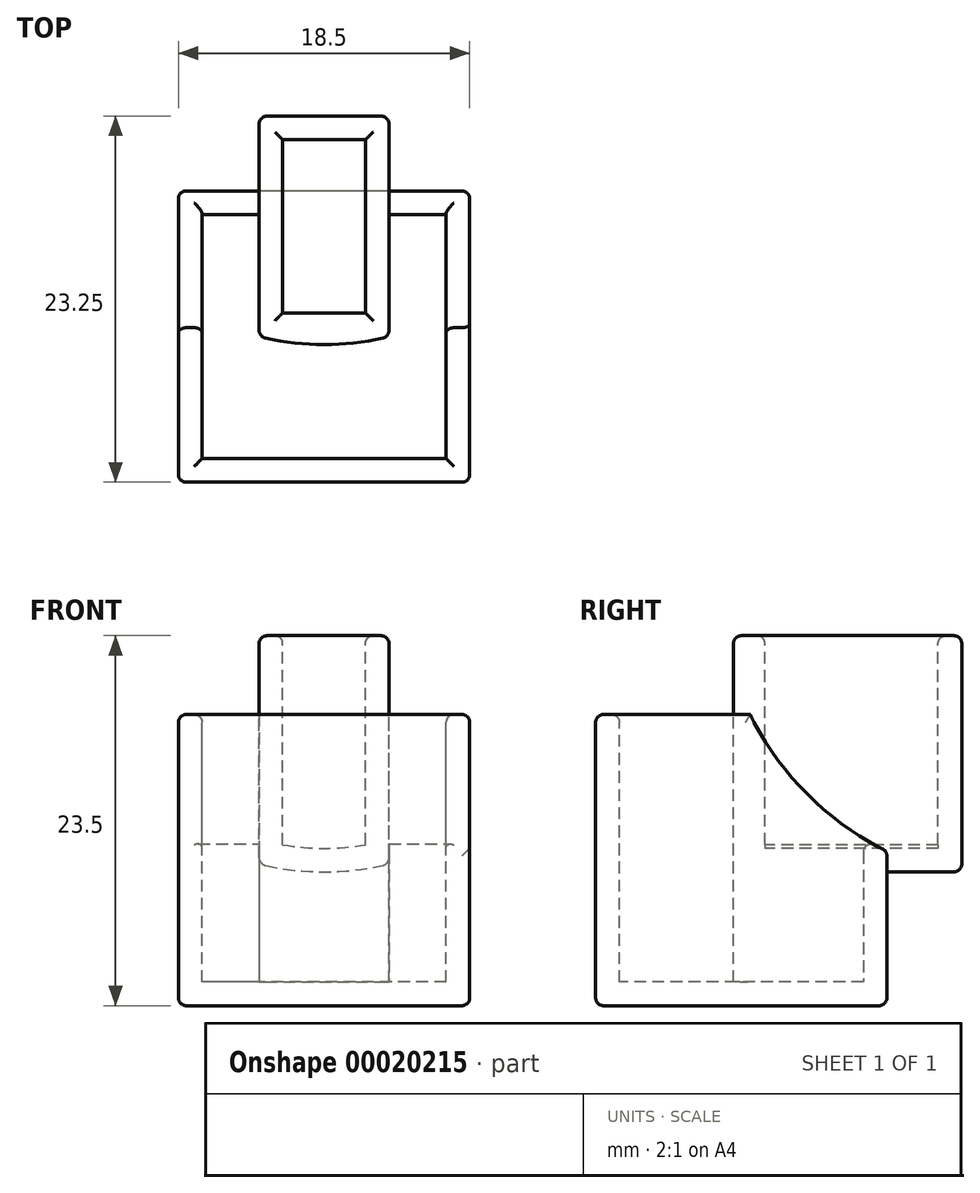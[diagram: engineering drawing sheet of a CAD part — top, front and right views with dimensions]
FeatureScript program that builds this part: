
annotation { "Feature Type Name" : "Feature", "Feature Type Description" : "" }
export const myFeature = defineFeature(function(context is Context, id is Id, definition is map)
    precondition{}
    {
        {
            var Q0;
            Q0=qCreatedBy(makeId("Top.planeOp"),FACE);
            var sketch = newSketch(context, id + "F0", { "sketchPlane" : qUnion([Q0])});
            skLineSegment(sketch, "E0.rect.bottom", {"start": v(9.25, 9.25) * mm, "end": v(-9.25, 9.25) * mm});
            skLineSegment(sketch, "E0.rect.top", {"start": v(9.25, -9.25) * mm, "end": v(-9.25, -9.25) * mm});
            skLineSegment(sketch, "E0.rect.left", {"start": v(9.25, 9.25) * mm, "end": v(9.25, -9.25) * mm});
            skLineSegment(sketch, "E0.rect.right", {"start": v(-9.25, 9.25) * mm, "end": v(-9.25, -9.25) * mm});
            skPoint(sketch, "E0.rect.middle", {"position": v(0, 0) * mm});
            skSolve(sketch);
        }
        {
            var Q0;
            Q0=makeQuery(id+"F0.imprint","IMPRINT",FACE,{"disambiguationData":[TD([[makeQuery(id+"F0.imprint","IMPRINT",EDGE,{"derivedFrom":sQuery(id+"F0.wireOp",EDGE,"E0.rect.bottom")}),1.0]])]});
            extrude(context, id + "F1", {"entities" : qUnion([Q0]), "oppositeDirection" : true, "depth" : 18.5 * mm});
        }
        {
            var Q0;
            Q0=makeQuery(id+"F1.opExtrude","SWEPT_FACE",FACE,{"disambiguationData":[OSD([sQuery(id+"F0.wireOp",EDGE,"E0.rect.left")])]});
            var sketch = newSketch(context, id + "F2", { "sketchPlane" : qUnion([Q0])});
            skPoint(sketch, "E1", {"position": v(2, 0) * mm});
            skPoint(sketch, "E2", {"position": v(-9.25, -18.5) * mm});
            skPoint(sketch, "E3", {"position": v(4.19, -5.06) * mm});
            skCircle(sketch, "E4", {"center": v(17.62, 8.37) * mm, "radius": 19 * mm});
            skSolve(sketch);
        }
        {
            var Q0;
            Q0=qSketchRegion(id+"F2",true);
            extrude(context, id + "F3", {"entities" : qUnion([Q0]), "operationType" : NewBodyOperationType.REMOVE, "oppositeDirection" : true, "depth" : 25.4 * mm});
        }
        {
            var Q0;
            Q0=makeQuery(id+"F1.opExtrude","CAP_FACE",FACE,{"disambiguationData":[OSD([sQuery(id+"F0.wireOp",EDGE,"E0.rect.bottom"),sQuery(id+"F0.wireOp",EDGE,"E0.rect.top"),sQuery(id+"F0.wireOp",EDGE,"E0.rect.left"),sQuery(id+"F0.wireOp",EDGE,"E0.rect.right")])],"isStart":true});
            var Q1;
            Q1=makeQuery(id+"F3.boolean.opBoolean","COPY",FACE,{"derivedFrom":makeQuery(id+"F3.opExtrude","SWEPT_FACE",FACE,{"disambiguationData":[OSD([sQuery(id+"F2.wireOp",EDGE,"E4")])]})});
            shell(context, id + "F4", {"entities" : qUnion([Q0, Q1]), "thickness" : 1.5 * mm});
        }
        {
            var Q0;
            Q0=qCreatedBy(makeId("Front.planeOp"),FACE);
            var sketch = newSketch(context, id + "F5", { "sketchPlane" : qUnion([Q0])});
            skPoint(sketch, "E5", {"position": v(0, 5) * mm});
            skLineSegment(sketch, "E6", {"start": v(0, 5) * mm, "end": v(0, -9.5) * mm});
            skLineSegment(sketch, "E7.top", {"start": v(4.12, 5) * mm, "end": v(-4.12, 5) * mm});
            skLineSegment(sketch, "E7.left", {"start": v(4.12, -9.5) * mm, "end": v(4.12, 5) * mm});
            skLineSegment(sketch, "E7.right", {"start": v(-4.12, -9.5) * mm, "end": v(-4.12, 5) * mm});
            skPoint(sketch, "E8", {"position": v(0, -10) * mm});
            skArc(sketch, "E9", {"start": v(-4.12, -9.5) * mm, "mid": v(0, -10) * mm, "end": v(4.13, -9.5) * mm});
            skSolve(sketch);
        }
        {
            var Q0;
            Q0=qSketchRegion(id+"F5",true);
            extrude(context, id + "F6", {"entities" : qUnion([Q0]), "operationType" : NewBodyOperationType.ADD, "oppositeDirection" : true, "depth" : 14 * mm});
        }
        {
            var Q0;
            Q0=makeQuery(id+"F6.opExtrude","SWEPT_FACE",FACE,{"disambiguationData":[OSD([sQuery(id+"F5.wireOp",EDGE,"E7.top")])]});
            shell(context, id + "F7", {"entities" : qUnion([Q0]), "thickness" : 1.5 * mm});
        }
        {
            var Q0;
            Q0=makeQuery(id+"F6.opExtrude","SWEPT_FACE",FACE,{"disambiguationData":[OSD([sQuery(id+"F5.wireOp",EDGE,"E7.top")])]});
            var sketch = newSketch(context, id + "F8", { "sketchPlane" : qUnion([Q0])});
            skArc(sketch, "E10", {"start": v(-4.13, 0) * mm, "mid": v(0, -0.5) * mm, "end": v(4.12, 0) * mm});
            skLineSegment(sketch, "E11", {"start": v(-4.13, 0) * mm, "end": v(4.12, 0) * mm});
            skSolve(sketch);
        }
        {
            var Q0;
            Q0=makeQuery(id+"F8.imprint","IMPRINT",FACE,{"disambiguationData":[TD([[makeQuery(id+"F8.imprint","IMPRINT",EDGE,{"derivedFrom":sQuery(id+"F8.wireOp",EDGE,"E10")}),1.0]])]});
            extrude(context, id + "F9", {"entities" : qUnion([Q0]), "operationType" : NewBodyOperationType.ADD, "oppositeDirection" : true, "depth" : 23.32 * mm});
        }
        {
            var Q0;
            Q0=makeQuery(id+"F9.opExtrude","SWEPT_FACE",FACE,{"disambiguationData":[OSD([sQuery(id+"F8.wireOp",EDGE,"E11")])]});
            extrude(context, id + "F10", {"entities" : qUnion([Q0]), "operationType" : NewBodyOperationType.ADD, "depth" : 8.55 * mm});
        }
        {
            var Q0;
            Q0=makeQuery(id+"F3.boolean.opBoolean","INTERSECT",EDGE,{"derivedFrom":[makeQuery(id+"F1.opExtrude","SWEPT_FACE",FACE,{"disambiguationData":[OSD([sQuery(id+"F0.wireOp",EDGE,"E0.rect.right")])]}),makeQuery(id+"F3.opExtrude","SWEPT_FACE",FACE,{"disambiguationData":[OSD([sQuery(id+"F2.wireOp",EDGE,"E4")])]})]});
            var Q1;
            Q1=makeQuery(id+"F1.opExtrude","CAP_EDGE",EDGE,{"disambiguationData":[OSD([sQuery(id+"F0.wireOp",EDGE,"E0.rect.right")])],"isStart":true});
            var Q2;
            Q2=makeQuery(id+"F1.opExtrude","SWEPT_EDGE",EDGE,{"disambiguationData":[OSD([sQuery(id+"F0.wireOp",EDGE,"E0.rect.top"),sQuery(id+"F0.wireOp",EDGE,"E0.rect.right")])]});
            var Q3;
            Q3=makeQuery(id+"F1.opExtrude","CAP_EDGE",EDGE,{"disambiguationData":[OSD([sQuery(id+"F0.wireOp",EDGE,"E0.rect.right")])],"isStart":false});
            var Q4;
            Q4=makeQuery(id+"F1.opExtrude","SWEPT_EDGE",EDGE,{"disambiguationData":[OSD([sQuery(id+"F0.wireOp",EDGE,"E0.rect.bottom"),sQuery(id+"F0.wireOp",EDGE,"E0.rect.right")])]});
            var Q5;
            Q5=makeQuery(id+"F6.opExtrude","SWEPT_EDGE",EDGE,{"disambiguationData":[OSD([sQuery(id+"F5.wireOp",EDGE,"E7.top"),sQuery(id+"F5.wireOp",EDGE,"E7.right")])]});
            var Q6;
            Q6=makeQuery(id+"F6.opExtrude","CAP_EDGE",EDGE,{"disambiguationData":[OSD([sQuery(id+"F5.wireOp",EDGE,"E7.right")])],"isStart":false});
            var Q7;
            Q7=makeQuery(id+"F6.opExtrude","CAP_EDGE",EDGE,{"disambiguationData":[OSD([sQuery(id+"F5.wireOp",EDGE,"E7.top")])],"isStart":false});
            var Q8;
            {var subQ0=sQuery(id+"F5.wireOp",EDGE,"E7.right");var subQ1=sQuery(id+"F5.wireOp",EDGE,"E9");Q8=makeQuery(id+"F6.boolean.opBoolean","SPLIT",EDGE,{"disambiguationData":[TD([makeQuery(id+"F1.opExtrude","SWEPT_FACE",FACE,{"disambiguationData":[OSD([sQuery(id+"F0.wireOp",EDGE,"E0.rect.bottom")])]})])],"derivedFrom":makeQuery(id+"F6.opExtrude","SWEPT_EDGE",EDGE,{"disambiguationData":[OSD([subQ0,subQ1])]})});}
            var Q9;
            {var subQ0=sQuery(id+"F0.wireOp",EDGE,"E0.rect.bottom");var subQ1=sQuery(id+"F2.wireOp",EDGE,"E4");Q9=makeQuery(id+"F6.boolean.opBoolean","SPLIT",EDGE,{"disambiguationData":[TD([makeQuery(id+"F4.opShell","OFFSET_FACE",FACE,{"disambiguationData":[OSD([sQuery(id+"F0.wireOp",EDGE,"E0.rect.right")])]})])],"derivedFrom":makeQuery(id+"F4.opShell","OFFSET_EDGE",EDGE,{"disambiguationData":[OSD([subQ0,subQ1])]})});}
            var Q10;
            Q10=makeQuery(id+"F4.opShell","OFFSET_EDGE",EDGE,{"disambiguationData":[OSD([sQuery(id+"F0.wireOp",EDGE,"E0.rect.right"),sQuery(id+"F2.wireOp",EDGE,"E4")])]});
            var Q11;
            {var subQ0=makeQuery(id+"F1.opExtrude","SWEPT_FACE",FACE,{"disambiguationData":[OSD([sQuery(id+"F0.wireOp",EDGE,"E0.rect.bottom")])]});var subQ1=makeQuery(id+"F3.opExtrude","SWEPT_FACE",FACE,{"disambiguationData":[OSD([sQuery(id+"F2.wireOp",EDGE,"E4")])]});Q11=makeQuery(id+"F6.boolean.opBoolean","SPLIT",EDGE,{"disambiguationData":[TD([makeQuery(id+"F1.opExtrude","SWEPT_FACE",FACE,{"disambiguationData":[OSD([sQuery(id+"F0.wireOp",EDGE,"E0.rect.right")])]})])],"derivedFrom":makeQuery(id+"F3.boolean.opBoolean","INTERSECT",EDGE,{"derivedFrom":[subQ0,subQ1]})});}
            var Q12;
            {var subQ0=sQuery(id+"F0.wireOp",EDGE,"E0.rect.right");Q12=makeQuery(id+"F4.opShell","OFFSET_EDGE",EDGE,{"disambiguationData":[OSD([subQ0]),TDD([makeQuery(id+"F1.opExtrude","CAP_EDGE",EDGE,{"disambiguationData":[OSD([subQ0])],"isStart":true})])]});}
            var Q13;
            {var subQ0=sQuery(id+"F0.wireOp",EDGE,"E0.rect.top");Q13=makeQuery(id+"F4.opShell","OFFSET_EDGE",EDGE,{"disambiguationData":[OSD([subQ0]),TDD([makeQuery(id+"F1.opExtrude","CAP_EDGE",EDGE,{"disambiguationData":[OSD([subQ0])],"isStart":true})])]});}
            var Q14;
            Q14=makeQuery(id+"F1.opExtrude","CAP_EDGE",EDGE,{"disambiguationData":[OSD([sQuery(id+"F0.wireOp",EDGE,"E0.rect.top")])],"isStart":true});
            var Q15;
            Q15=makeQuery(id+"F1.opExtrude","CAP_EDGE",EDGE,{"disambiguationData":[OSD([sQuery(id+"F0.wireOp",EDGE,"E0.rect.left")])],"isStart":true});
            var Q16;
            {var subQ0=sQuery(id+"F0.wireOp",EDGE,"E0.rect.left");Q16=makeQuery(id+"F4.opShell","OFFSET_EDGE",EDGE,{"disambiguationData":[OSD([subQ0]),TDD([makeQuery(id+"F1.opExtrude","CAP_EDGE",EDGE,{"disambiguationData":[OSD([subQ0])],"isStart":true})])]});}
            var Q17;
            Q17=makeQuery(id+"F3.boolean.opBoolean","COPY",EDGE,{"derivedFrom":makeQuery(id+"F3.opExtrude","CAP_EDGE",EDGE,{"disambiguationData":[OSD([sQuery(id+"F2.wireOp",EDGE,"E4")])],"isStart":true})});
            var Q18;
            Q18=makeQuery(id+"F4.opShell","OFFSET_EDGE",EDGE,{"disambiguationData":[OSD([sQuery(id+"F2.wireOp",EDGE,"E4")])]});
            var Q19;
            {var subQ0=sQuery(id+"F0.wireOp",EDGE,"E0.rect.bottom");var subQ1=sQuery(id+"F2.wireOp",EDGE,"E4");Q19=makeQuery(id+"F6.boolean.opBoolean","SPLIT",EDGE,{"disambiguationData":[TD([makeQuery(id+"F4.opShell","OFFSET_FACE",FACE,{"disambiguationData":[OSD([sQuery(id+"F0.wireOp",EDGE,"E0.rect.left")])]})])],"derivedFrom":makeQuery(id+"F4.opShell","OFFSET_EDGE",EDGE,{"disambiguationData":[OSD([subQ0,subQ1])]})});}
            var Q20;
            {var subQ0=makeQuery(id+"F1.opExtrude","SWEPT_FACE",FACE,{"disambiguationData":[OSD([sQuery(id+"F0.wireOp",EDGE,"E0.rect.bottom")])]});var subQ1=makeQuery(id+"F3.opExtrude","SWEPT_FACE",FACE,{"disambiguationData":[OSD([sQuery(id+"F2.wireOp",EDGE,"E4")])]});Q20=makeQuery(id+"F6.boolean.opBoolean","SPLIT",EDGE,{"disambiguationData":[TD([makeQuery(id+"F1.opExtrude","SWEPT_FACE",FACE,{"disambiguationData":[OSD([sQuery(id+"F0.wireOp",EDGE,"E0.rect.left")])]})])],"derivedFrom":makeQuery(id+"F3.boolean.opBoolean","INTERSECT",EDGE,{"derivedFrom":[subQ0,subQ1]})});}
            var Q21;
            Q21=makeQuery(id+"F1.opExtrude","CAP_EDGE",EDGE,{"disambiguationData":[OSD([sQuery(id+"F0.wireOp",EDGE,"E0.rect.bottom")])],"isStart":false});
            var Q22;
            Q22=makeQuery(id+"F1.opExtrude","SWEPT_EDGE",EDGE,{"disambiguationData":[OSD([sQuery(id+"F0.wireOp",EDGE,"E0.rect.bottom"),sQuery(id+"F0.wireOp",EDGE,"E0.rect.left")])]});
            var Q23;
            Q23=makeQuery(id+"F1.opExtrude","CAP_EDGE",EDGE,{"disambiguationData":[OSD([sQuery(id+"F0.wireOp",EDGE,"E0.rect.left")])],"isStart":false});
            var Q24;
            Q24=makeQuery(id+"F1.opExtrude","SWEPT_EDGE",EDGE,{"disambiguationData":[OSD([sQuery(id+"F0.wireOp",EDGE,"E0.rect.top"),sQuery(id+"F0.wireOp",EDGE,"E0.rect.left")])]});
            var Q25;
            Q25=makeQuery(id+"F6.opExtrude","SWEPT_EDGE",EDGE,{"disambiguationData":[OSD([sQuery(id+"F5.wireOp",EDGE,"E7.top"),sQuery(id+"F5.wireOp",EDGE,"E7.left")])]});
            var Q26;
            Q26=makeQuery(id+"F6.opExtrude","CAP_EDGE",EDGE,{"disambiguationData":[OSD([sQuery(id+"F5.wireOp",EDGE,"E7.left")])],"isStart":false});
            var Q27;
            Q27=makeQuery(id+"F1.opExtrude","CAP_EDGE",EDGE,{"disambiguationData":[OSD([sQuery(id+"F0.wireOp",EDGE,"E0.rect.top")])],"isStart":false});
            var Q28;
            Q28=makeQuery(id+"F9.opExtrude","CAP_EDGE",EDGE,{"disambiguationData":[OSD([sQuery(id+"F8.wireOp",EDGE,"E10")])],"isStart":true});
            var Q29;
            Q29=makeQuery(id+"F7.opShell","OFFSET_EDGE",EDGE,{"disambiguationData":[OSD([sQuery(id+"F5.wireOp",EDGE,"E7.top"),sQuery(id+"F5.wireOp",EDGE,"E7.right")])]});
            var Q30;
            {var subQ0=sQuery(id+"F5.wireOp",EDGE,"E7.top");Q30=makeQuery(id+"F7.opShell","OFFSET_EDGE",EDGE,{"disambiguationData":[OSD([subQ0]),TDD([makeQuery(id+"F6.opExtrude","CAP_EDGE",EDGE,{"disambiguationData":[OSD([subQ0])],"isStart":false})])]});}
            var Q31;
            Q31=makeQuery(id+"F7.opShell","OFFSET_EDGE",EDGE,{"disambiguationData":[OSD([sQuery(id+"F5.wireOp",EDGE,"E7.top"),sQuery(id+"F5.wireOp",EDGE,"E7.left")])]});
            var Q32;
            {var subQ0=sQuery(id+"F5.wireOp",EDGE,"E7.top");Q32=makeQuery(id+"F7.opShell","OFFSET_EDGE",EDGE,{"disambiguationData":[OSD([subQ0]),TDD([makeQuery(id+"F6.opExtrude","CAP_EDGE",EDGE,{"disambiguationData":[OSD([subQ0])],"isStart":true})])]});}
            var Q33;
            {var subQ0=sQuery(id+"F5.wireOp",EDGE,"E7.left");var subQ1=sQuery(id+"F5.wireOp",EDGE,"E9");Q33=makeQuery(id+"F6.boolean.opBoolean","SPLIT",EDGE,{"disambiguationData":[TD([makeQuery(id+"F1.opExtrude","SWEPT_FACE",FACE,{"disambiguationData":[OSD([sQuery(id+"F0.wireOp",EDGE,"E0.rect.bottom")])]})])],"derivedFrom":makeQuery(id+"F6.opExtrude","SWEPT_EDGE",EDGE,{"disambiguationData":[OSD([subQ0,subQ1])]})});}
            var Q34;
            Q34=makeQuery(id+"F6.opExtrude","CAP_EDGE",EDGE,{"disambiguationData":[OSD([sQuery(id+"F5.wireOp",EDGE,"E9")])],"isStart":false});
            var Q35;
            {var subQ0=sQuery(id+"F5.wireOp",EDGE,"E7.right");var subQ1=sQuery(id+"F5.wireOp",EDGE,"E7.top");var subQ2=sQuery(id+"F8.wireOp",EDGE,"E10");var subQ3=sQuery(id+"F8.wireOp",EDGE,"E11");var subQ4=makeQuery(id+"F9.opExtrude","SWEPT_EDGE",EDGE,{"disambiguationData":[OSD([subQ1,subQ0,subQ2,subQ3])]});Q35=makeQuery(id+"F10.boolean.opBoolean","MERGE",EDGE,{"derivedFrom":[makeQuery(id+"F9.boolean.opBoolean","MERGE",EDGE,{"derivedFrom":[makeQuery(id+"F6.opExtrude","CAP_EDGE",EDGE,{"disambiguationData":[OSD([subQ0])],"isStart":true}),subQ4]}),subQ4,makeQuery(id+"F10.opExtrude","CAP_EDGE",EDGE,{"disambiguationData":[OSD([subQ1,subQ0,subQ2,subQ3])],"isStart":true})]});}
            var Q36;
            {var subQ0=sQuery(id+"F5.wireOp",EDGE,"E7.left");var subQ1=sQuery(id+"F5.wireOp",EDGE,"E7.top");var subQ2=sQuery(id+"F8.wireOp",EDGE,"E10");var subQ3=sQuery(id+"F8.wireOp",EDGE,"E11");var subQ4=makeQuery(id+"F9.opExtrude","SWEPT_EDGE",EDGE,{"disambiguationData":[OSD([subQ1,subQ0,subQ2,subQ3])]});Q36=makeQuery(id+"F10.boolean.opBoolean","MERGE",EDGE,{"derivedFrom":[makeQuery(id+"F9.boolean.opBoolean","MERGE",EDGE,{"derivedFrom":[makeQuery(id+"F6.opExtrude","CAP_EDGE",EDGE,{"disambiguationData":[OSD([subQ0])],"isStart":true}),subQ4]}),subQ4,makeQuery(id+"F10.opExtrude","CAP_EDGE",EDGE,{"disambiguationData":[OSD([subQ1,subQ0,subQ2,subQ3])],"isStart":true})]});}
            fillet(context, id + "F11", {"entities" : qUnion([Q0, Q1, Q2, Q3, Q4, Q5, Q6, Q7, Q8, Q9, Q10, Q11, Q12, Q13, Q14, Q15, Q16, Q17, Q18, Q19, Q20, Q21, Q22, Q23, Q24, Q25, Q26, Q27, Q28, Q29, Q30, Q31, Q32, Q33, Q34, Q35, Q36]), "radius" : .5 * mm, "tangentPropagation" : true, "allowEdgeOverflow" : false});
        }
    });
